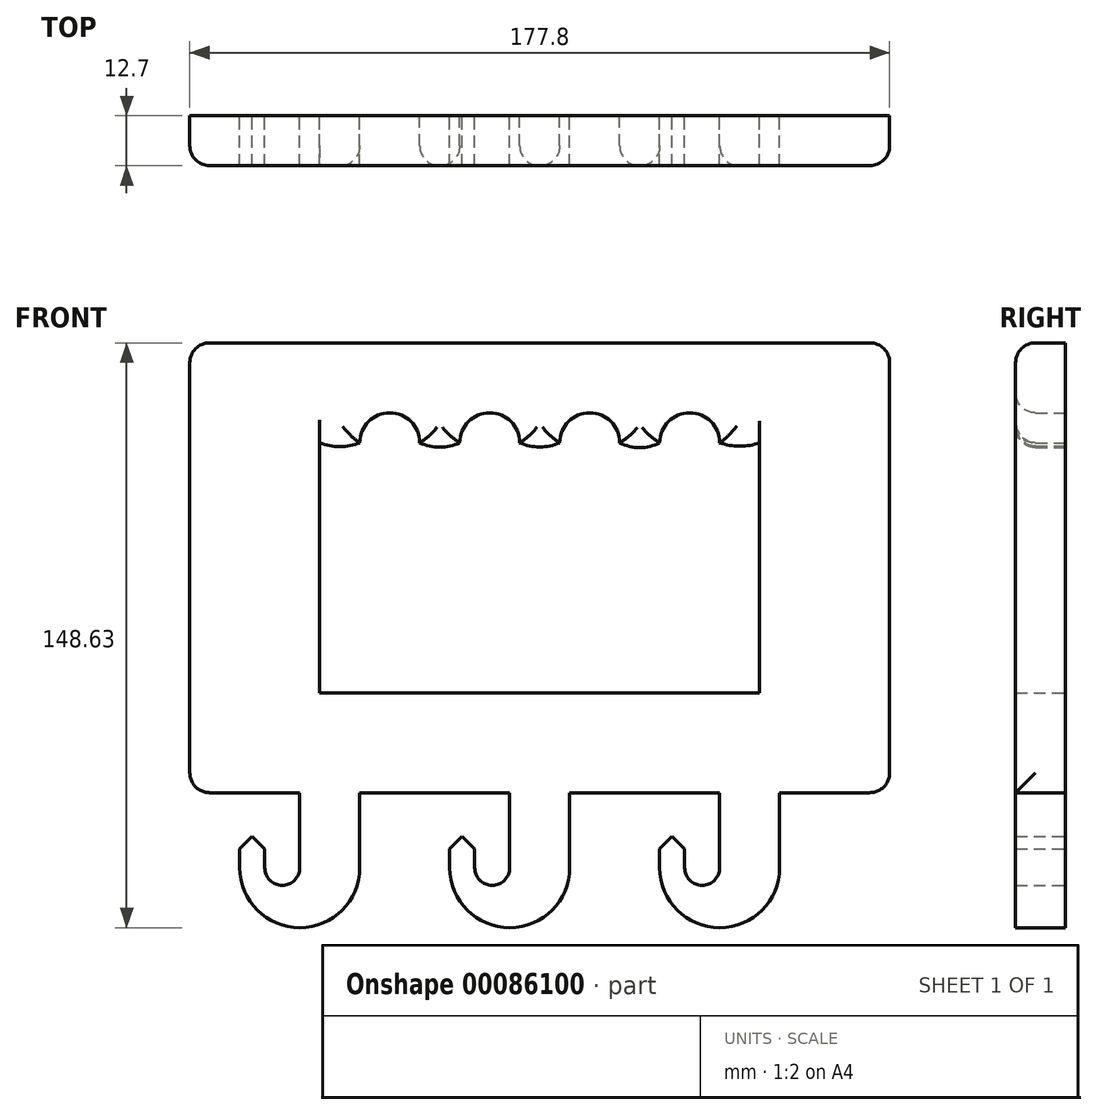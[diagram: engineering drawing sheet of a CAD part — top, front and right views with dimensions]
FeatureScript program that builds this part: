
annotation { "Feature Type Name" : "Feature", "Feature Type Description" : "" }
export const myFeature = defineFeature(function(context is Context, id is Id, definition is map)
    precondition{}
    {
        {
            var Q0;
            Q0=qCreatedBy(makeId("Front.planeOp"),FACE);
            var sketch = newSketch(context, id + "F0", { "sketchPlane" : qUnion([Q0])});
            skLineSegment(sketch, "E0.bottom", {"start": v(88.9, 57.15) * mm, "end": v(-88.9, 57.15) * mm});
            skLineSegment(sketch, "E0.top", {"start": v(88.9, -57.15) * mm, "end": v(60.96, -57.15) * mm});
            skLineSegment(sketch, "E0.left", {"start": v(88.9, 57.15) * mm, "end": v(88.9, -57.15) * mm});
            skLineSegment(sketch, "E0.right", {"start": v(-88.9, 57.15) * mm, "end": v(-88.9, -57.15) * mm});
            skPoint(sketch, "E0.middle", {"position": v(0, 0) * mm});
            skLineSegment(sketch, "E1.top", {"start": v(-55.88, -31.75) * mm, "end": v(55.88, -31.75) * mm});
            skLineSegment(sketch, "E1.left", {"start": v(-55.88, 31.75) * mm, "end": v(-55.88, -31.75) * mm});
            skLineSegment(sketch, "E1.right", {"start": v(55.88, 31.75) * mm, "end": v(55.88, -31.75) * mm});
            skArc(sketch, "E2", {"start": v(-55.88, 31.75) * mm, "mid": v(-50.8, 30.77) * mm, "end": v(-45.72, 31.75) * mm});
            skArc(sketch, "E3", {"start": v(-30.48, 31.75) * mm, "mid": v(-38.1, 39.37) * mm, "end": v(-45.72, 31.75) * mm});
            skArc(sketch, "E4", {"start": v(-30.48, 31.75) * mm, "mid": v(-25.4, 30.66) * mm, "end": v(-20.32, 31.75) * mm});
            skArc(sketch, "E5", {"start": v(-5.08, 31.75) * mm, "mid": v(-12.7, 39.37) * mm, "end": v(-20.32, 31.75) * mm});
            skArc(sketch, "E6", {"start": v(-5.08, 31.75) * mm, "mid": v(0, 30.68) * mm, "end": v(5.08, 31.75) * mm});
            skArc(sketch, "E7", {"start": v(20.32, 31.75) * mm, "mid": v(12.7, 39.37) * mm, "end": v(5.08, 31.75) * mm});
            skArc(sketch, "E8", {"start": v(20.32, 31.75) * mm, "mid": v(25.4, 30.53) * mm, "end": v(30.48, 31.75) * mm});
            skArc(sketch, "E9", {"start": v(45.72, 31.75) * mm, "mid": v(38.1, 39.37) * mm, "end": v(30.48, 31.75) * mm});
            skArc(sketch, "E10", {"start": v(45.72, 31.75) * mm, "mid": v(50.8, 30.9) * mm, "end": v(55.88, 31.75) * mm});
            skLineSegment(sketch, "E11.left", {"start": v(-60.96, -57.15) * mm, "end": v(-60.96, -76.24) * mm});
            skLineSegment(sketch, "E11.right", {"start": v(-45.72, -57.15) * mm, "end": v(-45.72, -76.24) * mm});
            skLineSegment(sketch, "E12.left", {"start": v(7.62, -57.15) * mm, "end": v(7.62, -76.24) * mm});
            skLineSegment(sketch, "E12.right", {"start": v(-7.62, -57.15) * mm, "end": v(-7.62, -76.24) * mm});
            skLineSegment(sketch, "E13.left", {"start": v(60.96, -57.15) * mm, "end": v(60.96, -76.24) * mm});
            skLineSegment(sketch, "E13.right", {"start": v(45.72, -57.15) * mm, "end": v(45.72, -76.24) * mm});
            skArc(sketch, "E14", {"start": v(-76.2, -76.24) * mm, "mid": v(-60.96, -91.48) * mm, "end": v(-45.72, -76.24) * mm});
            skArc(sketch, "E15", {"start": v(-22.86, -76.24) * mm, "mid": v(-7.62, -91.48) * mm, "end": v(7.62, -76.24) * mm});
            skArc(sketch, "E16", {"start": v(30.48, -76.24) * mm, "mid": v(45.72, -91.48) * mm, "end": v(60.96, -76.24) * mm});
            skLineSegment(sketch, "E17.top", {"start": v(-76.2, -66.4) * mm, "end": v(-69.85, -66.4) * mm});
            skLineSegment(sketch, "E17.left", {"start": v(-76.2, -76.24) * mm, "end": v(-76.2, -66.4) * mm});
            skLineSegment(sketch, "E17.right", {"start": v(-69.85, -76.24) * mm, "end": v(-69.85, -66.4) * mm});
            skLineSegment(sketch, "E18.top", {"start": v(-22.86, -66.4) * mm, "end": v(-16.5, -66.4) * mm});
            skLineSegment(sketch, "E18.left", {"start": v(-22.86, -76.24) * mm, "end": v(-22.86, -66.4) * mm});
            skLineSegment(sketch, "E18.right", {"start": v(-16.5, -76.24) * mm, "end": v(-16.5, -66.4) * mm});
            skLineSegment(sketch, "E19.top", {"start": v(30.48, -66.4) * mm, "end": v(36.83, -66.4) * mm});
            skLineSegment(sketch, "E19.left", {"start": v(30.48, -76.24) * mm, "end": v(30.48, -66.4) * mm});
            skLineSegment(sketch, "E19.right", {"start": v(36.83, -76.24) * mm, "end": v(36.83, -66.4) * mm});
            skArc(sketch, "E20", {"start": v(-69.85, -76.24) * mm, "mid": v(-65.4, -80.68) * mm, "end": v(-60.96, -76.24) * mm});
            skArc(sketch, "E21", {"start": v(-16.5, -76.24) * mm, "mid": v(-12.07, -80.68) * mm, "end": v(-7.62, -76.24) * mm});
            skArc(sketch, "E22", {"start": v(36.83, -76.24) * mm, "mid": v(41.28, -80.68) * mm, "end": v(45.72, -76.24) * mm});
            skLineSegment(sketch, "E23.trimOffspring", {"start": v(-60.96, -57.15) * mm, "end": v(-88.9, -57.15) * mm});
            skLineSegment(sketch, "E24.trimOffspring", {"start": v(-7.62, -57.15) * mm, "end": v(-45.72, -57.15) * mm});
            skLineSegment(sketch, "E25.trimOffspring", {"start": v(45.72, -57.15) * mm, "end": v(7.62, -57.15) * mm});
            skSolve(sketch);
        }
        {
            var Q0;
            Q0=makeQuery(id+"F0.imprint","IMPRINT",FACE,{"disambiguationData":[TD([[makeQuery(id+"F0.imprint","IMPRINT",EDGE,{"derivedFrom":sQuery(id+"F0.wireOp",EDGE,"E0.bottom")}),1.0]])]});
            extrude(context, id + "F1", {"entities" : qUnion([Q0]), "depth" : 12.7 * mm});
        }
        {
            var Q0;
            Q0=makeQuery(id+"F1.opExtrude","CAP_EDGE",EDGE,{"disambiguationData":[OSD([sQuery(id+"F0.wireOp",EDGE,"E2")])],"isStart":false});
            var Q1;
            Q1=makeQuery(id+"F1.opExtrude","CAP_EDGE",EDGE,{"disambiguationData":[OSD([sQuery(id+"F0.wireOp",EDGE,"E3")])],"isStart":false});
            var Q2;
            Q2=makeQuery(id+"F1.opExtrude","CAP_EDGE",EDGE,{"disambiguationData":[OSD([sQuery(id+"F0.wireOp",EDGE,"E4")])],"isStart":false});
            var Q3;
            Q3=makeQuery(id+"F1.opExtrude","CAP_EDGE",EDGE,{"disambiguationData":[OSD([sQuery(id+"F0.wireOp",EDGE,"E5")])],"isStart":false});
            var Q4;
            Q4=makeQuery(id+"F1.opExtrude","CAP_EDGE",EDGE,{"disambiguationData":[OSD([sQuery(id+"F0.wireOp",EDGE,"E6")])],"isStart":false});
            var Q5;
            Q5=makeQuery(id+"F1.opExtrude","CAP_EDGE",EDGE,{"disambiguationData":[OSD([sQuery(id+"F0.wireOp",EDGE,"E7")])],"isStart":false});
            var Q6;
            Q6=makeQuery(id+"F1.opExtrude","CAP_EDGE",EDGE,{"disambiguationData":[OSD([sQuery(id+"F0.wireOp",EDGE,"E8")])],"isStart":false});
            var Q7;
            Q7=makeQuery(id+"F1.opExtrude","CAP_EDGE",EDGE,{"disambiguationData":[OSD([sQuery(id+"F0.wireOp",EDGE,"E9")])],"isStart":false});
            var Q8;
            Q8=makeQuery(id+"F1.opExtrude","CAP_EDGE",EDGE,{"disambiguationData":[OSD([sQuery(id+"F0.wireOp",EDGE,"E10")])],"isStart":false});
            var Q9;
            Q9=makeQuery(id+"F1.opExtrude","SWEPT_EDGE",EDGE,{"disambiguationData":[OSD([sQuery(id+"F0.wireOp",EDGE,"E0.bottom"),sQuery(id+"F0.wireOp",EDGE,"E0.left")])]});
            var Q10;
            Q10=makeQuery(id+"F1.opExtrude","SWEPT_EDGE",EDGE,{"disambiguationData":[OSD([sQuery(id+"F0.wireOp",EDGE,"E0.top"),sQuery(id+"F0.wireOp",EDGE,"E0.left")])]});
            var Q11;
            Q11=makeQuery(id+"F1.opExtrude","CAP_EDGE",EDGE,{"disambiguationData":[OSD([sQuery(id+"F0.wireOp",EDGE,"E0.left")])],"isStart":false});
            var Q12;
            Q12=makeQuery(id+"F1.opExtrude","CAP_EDGE",EDGE,{"disambiguationData":[OSD([sQuery(id+"F0.wireOp",EDGE,"E0.right")])],"isStart":false});
            var Q13;
            Q13=makeQuery(id+"F1.opExtrude","SWEPT_EDGE",EDGE,{"disambiguationData":[OSD([sQuery(id+"F0.wireOp",EDGE,"E0.bottom"),sQuery(id+"F0.wireOp",EDGE,"E0.right")])]});
            var Q14;
            Q14=makeQuery(id+"F1.opExtrude","SWEPT_EDGE",EDGE,{"disambiguationData":[OSD([sQuery(id+"F0.wireOp",EDGE,"E0.right"),sQuery(id+"F0.wireOp",EDGE,"E23.trimOffspring")])]});
            var Q15;
            Q15=makeQuery(id+"F1.opExtrude","CAP_EDGE",EDGE,{"disambiguationData":[OSD([sQuery(id+"F0.wireOp",EDGE,"E0.bottom")])],"isStart":false});
            fillet(context, id + "F2", {"entities" : qUnion([Q0, Q1, Q2, Q3, Q4, Q5, Q6, Q7, Q8, Q9, Q10, Q11, Q12, Q13, Q14, Q15]), "radius" : 5.08 * mm, "tangentPropagation" : true, "allowEdgeOverflow" : false});
        }
        {
            var Q0;
            Q0=makeQuery(id+"F1.opExtrude","SWEPT_EDGE",EDGE,{"disambiguationData":[OSD([sQuery(id+"F0.wireOp",EDGE,"E17.top"),sQuery(id+"F0.wireOp",EDGE,"E17.right")])]});
            var Q1;
            Q1=makeQuery(id+"F1.opExtrude","SWEPT_EDGE",EDGE,{"disambiguationData":[OSD([sQuery(id+"F0.wireOp",EDGE,"E17.top"),sQuery(id+"F0.wireOp",EDGE,"E17.left")])]});
            var Q2;
            Q2=makeQuery(id+"F1.opExtrude","SWEPT_EDGE",EDGE,{"disambiguationData":[OSD([sQuery(id+"F0.wireOp",EDGE,"E18.top"),sQuery(id+"F0.wireOp",EDGE,"E18.right")])]});
            var Q3;
            Q3=makeQuery(id+"F1.opExtrude","SWEPT_EDGE",EDGE,{"disambiguationData":[OSD([sQuery(id+"F0.wireOp",EDGE,"E18.top"),sQuery(id+"F0.wireOp",EDGE,"E18.left")])]});
            var Q4;
            Q4=makeQuery(id+"F1.opExtrude","SWEPT_EDGE",EDGE,{"disambiguationData":[OSD([sQuery(id+"F0.wireOp",EDGE,"E19.top"),sQuery(id+"F0.wireOp",EDGE,"E19.right")])]});
            var Q5;
            Q5=makeQuery(id+"F1.opExtrude","SWEPT_EDGE",EDGE,{"disambiguationData":[OSD([sQuery(id+"F0.wireOp",EDGE,"E19.top"),sQuery(id+"F0.wireOp",EDGE,"E19.left")])]});
            chamfer(context, id + "F3", {"entities" : qUnion([Q0, Q1, Q2, Q3, Q4, Q5]), "width" : 5.08 * mm, "tangentPropagation" : true});
        }
    });
